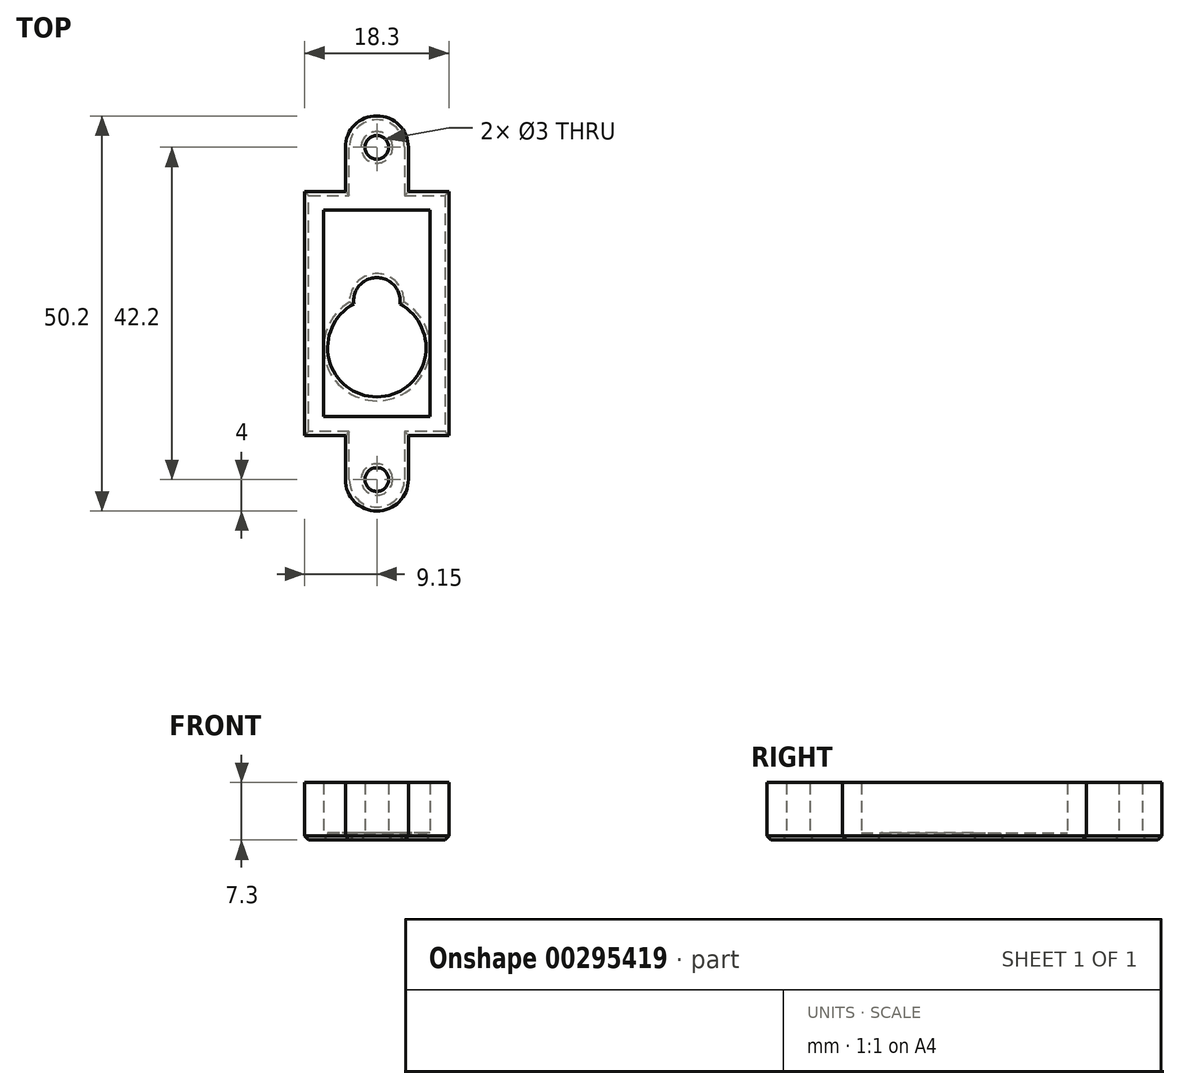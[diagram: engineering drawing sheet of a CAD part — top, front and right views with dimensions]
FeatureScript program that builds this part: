
annotation { "Feature Type Name" : "Feature", "Feature Type Description" : "" }
export const myFeature = defineFeature(function(context is Context, id is Id, definition is map)
    precondition{}
    {
        {
            var Q0;
            Q0=qCreatedBy(makeId("Top.planeOp"),FACE);
            var sketch = newSketch(context, id + "F0", { "sketchPlane" : qUnion([Q0])});
            skLineSegment(sketch, "E0.bottom", {"start": v(6.75, -13.1) * mm, "end": v(-6.75, -13.1) * mm});
            skLineSegment(sketch, "E0.top", {"start": v(6.75, 13.1) * mm, "end": v(-6.75, 13.1) * mm});
            skLineSegment(sketch, "E0.left", {"start": v(6.75, -13.1) * mm, "end": v(6.75, 13.1) * mm});
            skLineSegment(sketch, "E0.right", {"start": v(-6.75, -13.1) * mm, "end": v(-6.75, 13.1) * mm});
            skPoint(sketch, "E0.middle", {"position": v(0, 0) * mm});
            skLineSegment(sketch, "E1", {"start": v(-6.75, -11) * mm, "end": v(6.75, -11) * mm, "construction": true});
            skLineSegment(sketch, "E2", {"start": v(-6.75, 11) * mm, "end": v(6.75, 11) * mm, "construction": true});
            skArc(sketch, "E3", {"start": v(-2.92, 1.18) * mm, "mid": v(0, -10.6) * mm, "end": v(2.92, 1.18) * mm});
            skArc(sketch, "E4", {"start": v(2.92, 1.18) * mm, "mid": v(0, 4.55) * mm, "end": v(-2.92, 1.18) * mm});
            skSolve(sketch);
        }
        {
            var Q0;
            Q0 = qSketchRegion(id + "F0", true);
            extrude(context, id + "F1", {"entities" : qUnion([Q0]), "depth" : 2 * mm});
        }
        {
            var Q0;
            Q0=qCreatedBy(makeId("Top.planeOp"),FACE);
            var sketch = newSketch(context, id + "F2", { "sketchPlane" : qUnion([Q0])});
            skLineSegment(sketch, "E5", {"start": v(9.15, 15.5) * mm, "end": v(9.15, -15.5) * mm});
            skLineSegment(sketch, "E6", {"start": v(-9.15, 15.5) * mm, "end": v(-9.15, -15.5) * mm});
            skLineSegment(sketch, "E7", {"start": v(-9.15, 15.5) * mm, "end": v(9.15, 15.5) * mm});
            skLineSegment(sketch, "E8", {"start": v(9.15, -15.5) * mm, "end": v(-9.15, -15.5) * mm});
            skLineSegment(sketch, "E9.0", {"start": v(6.75, -13.1) * mm, "end": v(-6.75, -13.1) * mm});
            skLineSegment(sketch, "E10.0", {"start": v(6.75, -13.1) * mm, "end": v(6.75, 13.1) * mm});
            skLineSegment(sketch, "E11.0", {"start": v(6.75, 13.1) * mm, "end": v(-6.75, 13.1) * mm});
            skLineSegment(sketch, "E12.0", {"start": v(-6.75, -13.1) * mm, "end": v(-6.75, 13.1) * mm});
            skSolve(sketch);
        }
        {
            var Q0;
            Q0 = qSketchRegion(id + "F2", true);
            extrude(context, id + "F3", {"entities" : qUnion([Q0]), "operationType" : NewBodyOperationType.ADD, "depth" : (2 + 6.4) * mm});
        }
        {
            var Q0;
            Q0=qCreatedBy(makeId("Top.planeOp"),FACE);
            var sketch = newSketch(context, id + "F4", { "sketchPlane" : qUnion([Q0])});
            skLineSegment(sketch, "E13.0", {"start": v(-9.15, 15.5) * mm, "end": v(9.15, 15.5) * mm});
            skLineSegment(sketch, "E14.0", {"start": v(4, -15.5) * mm, "end": v(-4, -15.5) * mm});
            skLineSegment(sketch, "E15.0", {"start": v(9.15, -17.1) * mm, "end": v(4, -17.1) * mm, "construction": true});
            skArc(sketch, "E16", {"start": v(-4, -21.1) * mm, "mid": v(0, -25.1) * mm, "end": v(4, -21.1) * mm});
            skLineSegment(sketch, "E17", {"start": v(4, -15.5) * mm, "end": v(4, -21.1) * mm});
            skLineSegment(sketch, "E18", {"start": v(-4, -15.5) * mm, "end": v(-4, -21.1) * mm});
            skPoint(sketch, "E19.orphan", {"position": v(9.15, -15.5) * mm});
            skPoint(sketch, "E20.orphan", {"position": v(-9.15, -15.5) * mm});
            skLineSegment(sketch, "E21.MirrorCS", {"start": v(4, 15.5) * mm, "end": v(-4, 15.5) * mm});
            skArc(sketch, "E22.MirrorCS", {"start": v(-4, 21.1) * mm, "mid": v(0, 25.1) * mm, "end": v(4, 21.1) * mm});
            skLineSegment(sketch, "E23.MirrorCS", {"start": v(4, 15.5) * mm, "end": v(4, 21.1) * mm});
            skLineSegment(sketch, "E24.MirrorCS", {"start": v(-4, 15.5) * mm, "end": v(-4, 21.1) * mm});
            skCircle(sketch, "E25", {"center": v(0, 21.1) * mm, "radius": 1.5 * mm});
            skCircle(sketch, "E26", {"center": v(0, -21.1) * mm, "radius": 1.5 * mm});
            skSolve(sketch);
        }
        {
            var Q0;
            Q0 = qSketchRegion(id + "F4", true);
            var Q1;
            Q1=makeQuery(id+"F3.opExtrude","CAP_FACE",FACE,{"disambiguationData":[OSD([sQuery(id+"F2.wireOp",EDGE,"E5"),sQuery(id+"F2.wireOp",EDGE,"E6"),sQuery(id+"F2.wireOp",EDGE,"E7"),sQuery(id+"F2.wireOp",EDGE,"E8"),sQuery(id+"F2.wireOp",EDGE,"E9.0"),sQuery(id+"F2.wireOp",EDGE,"E10.0"),sQuery(id+"F2.wireOp",EDGE,"E11.0"),sQuery(id+"F2.wireOp",EDGE,"E12.0")])],"isStart":false});
            extrude(context, id + "F5", {"entities" : qUnion([Q0]), "operationType" : NewBodyOperationType.ADD, "endBound" : BoundingType.UP_TO_SURFACE, "endBoundEntityFace" : qUnion([Q1]), "depth" : 25 * mm});
        }
        {
            var Q0;
            Q0=makeQuery(id+"F5.boolean.opBoolean","MERGE",FACE,{"derivedFrom":[makeQuery(id+"F3.boolean.opBoolean","MERGE",FACE,{"derivedFrom":[makeQuery(id+"F1.opExtrude","CAP_FACE",FACE,{"disambiguationData":[OSD([sQuery(id+"F0.wireOp",EDGE,"E0.bottom"),sQuery(id+"F0.wireOp",EDGE,"E0.top"),sQuery(id+"F0.wireOp",EDGE,"E0.left"),sQuery(id+"F0.wireOp",EDGE,"E0.right"),sQuery(id+"F0.wireOp",EDGE,"E3"),sQuery(id+"F0.wireOp",EDGE,"E4")])],"isStart":true}),makeQuery(id+"F3.opExtrude","CAP_FACE",FACE,{"disambiguationData":[OSD([sQuery(id+"F2.wireOp",EDGE,"E5"),sQuery(id+"F2.wireOp",EDGE,"E6"),sQuery(id+"F2.wireOp",EDGE,"E7"),sQuery(id+"F2.wireOp",EDGE,"E8"),sQuery(id+"F2.wireOp",EDGE,"E9.0"),sQuery(id+"F2.wireOp",EDGE,"E10.0"),sQuery(id+"F2.wireOp",EDGE,"E11.0"),sQuery(id+"F2.wireOp",EDGE,"E12.0")])],"isStart":true})]}),makeQuery(id+"F5.opExtrude","CAP_FACE",FACE,{"disambiguationData":[OSD([sQuery(id+"F4.wireOp",EDGE,"E14.0"),sQuery(id+"F4.wireOp",EDGE,"E16"),sQuery(id+"F4.wireOp",EDGE,"E17"),sQuery(id+"F4.wireOp",EDGE,"E18"),sQuery(id+"F4.wireOp",EDGE,"E26")])],"isStart":true}),makeQuery(id+"F5.opExtrude","CAP_FACE",FACE,{"disambiguationData":[OSD([sQuery(id+"F4.wireOp",EDGE,"E21.MirrorCS"),sQuery(id+"F4.wireOp",EDGE,"E22.MirrorCS"),sQuery(id+"F4.wireOp",EDGE,"E23.MirrorCS"),sQuery(id+"F4.wireOp",EDGE,"E24.MirrorCS"),sQuery(id+"F4.wireOp",EDGE,"E25")])],"isStart":true})]});
            extrude(context, id + "F6", {"entities" : qUnion([Q0]), "operationType" : NewBodyOperationType.ADD, "depth" : 2.4 * mm});
        }
        {
            var Q0;
            Q0=makeQuery(id+"F6.opExtrude","CAP_FACE",FACE,{"disambiguationData":[OSD([sQuery(id+"F0.wireOp",EDGE,"E0.bottom"),sQuery(id+"F0.wireOp",EDGE,"E0.top"),sQuery(id+"F0.wireOp",EDGE,"E0.left"),sQuery(id+"F0.wireOp",EDGE,"E0.right"),sQuery(id+"F0.wireOp",EDGE,"E3"),sQuery(id+"F0.wireOp",EDGE,"E4"),sQuery(id+"F2.wireOp",EDGE,"E5"),sQuery(id+"F2.wireOp",EDGE,"E6"),sQuery(id+"F2.wireOp",EDGE,"E7"),sQuery(id+"F2.wireOp",EDGE,"E8"),sQuery(id+"F2.wireOp",EDGE,"E9.0"),sQuery(id+"F2.wireOp",EDGE,"E10.0"),sQuery(id+"F2.wireOp",EDGE,"E11.0"),sQuery(id+"F2.wireOp",EDGE,"E12.0"),sQuery(id+"F4.wireOp",EDGE,"E14.0"),sQuery(id+"F4.wireOp",EDGE,"E16"),sQuery(id+"F4.wireOp",EDGE,"E17"),sQuery(id+"F4.wireOp",EDGE,"E18"),sQuery(id+"F4.wireOp",EDGE,"E21.MirrorCS"),sQuery(id+"F4.wireOp",EDGE,"E22.MirrorCS"),sQuery(id+"F4.wireOp",EDGE,"E23.MirrorCS"),sQuery(id+"F4.wireOp",EDGE,"E24.MirrorCS"),sQuery(id+"F4.wireOp",EDGE,"E25"),sQuery(id+"F4.wireOp",EDGE,"E26")])],"isStart":false});
            extrude(context, id + "F7", {"entities" : qUnion([Q0]), "operationType" : NewBodyOperationType.REMOVE, "oppositeDirection" : true, "depth" : 2 * mm});
        }
        {
            var Q0;
            Q0=makeQuery(id+"F7.boolean.opBoolean","COPY",FACE,{"derivedFrom":makeQuery(id+"F7.opExtrude","CAP_FACE",FACE,{"disambiguationData":[OSD([sQuery(id+"F0.wireOp",EDGE,"E0.bottom"),sQuery(id+"F0.wireOp",EDGE,"E0.top"),sQuery(id+"F0.wireOp",EDGE,"E0.left"),sQuery(id+"F0.wireOp",EDGE,"E0.right"),sQuery(id+"F0.wireOp",EDGE,"E3"),sQuery(id+"F0.wireOp",EDGE,"E4"),sQuery(id+"F2.wireOp",EDGE,"E5"),sQuery(id+"F2.wireOp",EDGE,"E6"),sQuery(id+"F2.wireOp",EDGE,"E7"),sQuery(id+"F2.wireOp",EDGE,"E8"),sQuery(id+"F2.wireOp",EDGE,"E9.0"),sQuery(id+"F2.wireOp",EDGE,"E10.0"),sQuery(id+"F2.wireOp",EDGE,"E11.0"),sQuery(id+"F2.wireOp",EDGE,"E12.0"),sQuery(id+"F4.wireOp",EDGE,"E14.0"),sQuery(id+"F4.wireOp",EDGE,"E16"),sQuery(id+"F4.wireOp",EDGE,"E17"),sQuery(id+"F4.wireOp",EDGE,"E18"),sQuery(id+"F4.wireOp",EDGE,"E21.MirrorCS"),sQuery(id+"F4.wireOp",EDGE,"E22.MirrorCS"),sQuery(id+"F4.wireOp",EDGE,"E23.MirrorCS"),sQuery(id+"F4.wireOp",EDGE,"E24.MirrorCS"),sQuery(id+"F4.wireOp",EDGE,"E25"),sQuery(id+"F4.wireOp",EDGE,"E26")])],"isStart":false})});
            extrude(context, id + "F8", {"entities" : qUnion([Q0]), "operationType" : NewBodyOperationType.REMOVE, "oppositeDirection" : true, "depth" : 2 * mm});
        }
        {
            var Q0;
            Q0=makeQuery(id+"F8.boolean.opBoolean","COPY",FACE,{"derivedFrom":makeQuery(id+"F8.opExtrude","CAP_FACE",FACE,{"disambiguationData":[OSD([sQuery(id+"F0.wireOp",EDGE,"E0.bottom"),sQuery(id+"F0.wireOp",EDGE,"E0.top"),sQuery(id+"F0.wireOp",EDGE,"E0.left"),sQuery(id+"F0.wireOp",EDGE,"E0.right"),sQuery(id+"F0.wireOp",EDGE,"E3"),sQuery(id+"F0.wireOp",EDGE,"E4"),sQuery(id+"F2.wireOp",EDGE,"E5"),sQuery(id+"F2.wireOp",EDGE,"E6"),sQuery(id+"F2.wireOp",EDGE,"E7"),sQuery(id+"F2.wireOp",EDGE,"E8"),sQuery(id+"F2.wireOp",EDGE,"E9.0"),sQuery(id+"F2.wireOp",EDGE,"E10.0"),sQuery(id+"F2.wireOp",EDGE,"E11.0"),sQuery(id+"F2.wireOp",EDGE,"E12.0"),sQuery(id+"F4.wireOp",EDGE,"E14.0"),sQuery(id+"F4.wireOp",EDGE,"E16"),sQuery(id+"F4.wireOp",EDGE,"E17"),sQuery(id+"F4.wireOp",EDGE,"E18"),sQuery(id+"F4.wireOp",EDGE,"E21.MirrorCS"),sQuery(id+"F4.wireOp",EDGE,"E22.MirrorCS"),sQuery(id+"F4.wireOp",EDGE,"E23.MirrorCS"),sQuery(id+"F4.wireOp",EDGE,"E24.MirrorCS"),sQuery(id+"F4.wireOp",EDGE,"E25"),sQuery(id+"F4.wireOp",EDGE,"E26")])],"isStart":false})});
            extrude(context, id + "F9", {"entities" : qUnion([Q0]), "operationType" : NewBodyOperationType.ADD, "depth" : 1 * mm});
        }
        {
            var Q0;
            Q0=makeQuery(id+"F9.opExtrude","CAP_FACE",FACE,{"disambiguationData":[OSD([sQuery(id+"F0.wireOp",EDGE,"E0.bottom"),sQuery(id+"F0.wireOp",EDGE,"E0.top"),sQuery(id+"F0.wireOp",EDGE,"E0.left"),sQuery(id+"F0.wireOp",EDGE,"E0.right"),sQuery(id+"F0.wireOp",EDGE,"E3"),sQuery(id+"F0.wireOp",EDGE,"E4"),sQuery(id+"F2.wireOp",EDGE,"E5"),sQuery(id+"F2.wireOp",EDGE,"E6"),sQuery(id+"F2.wireOp",EDGE,"E7"),sQuery(id+"F2.wireOp",EDGE,"E8"),sQuery(id+"F2.wireOp",EDGE,"E9.0"),sQuery(id+"F2.wireOp",EDGE,"E10.0"),sQuery(id+"F2.wireOp",EDGE,"E11.0"),sQuery(id+"F2.wireOp",EDGE,"E12.0"),sQuery(id+"F4.wireOp",EDGE,"E14.0"),sQuery(id+"F4.wireOp",EDGE,"E16"),sQuery(id+"F4.wireOp",EDGE,"E17"),sQuery(id+"F4.wireOp",EDGE,"E18"),sQuery(id+"F4.wireOp",EDGE,"E21.MirrorCS"),sQuery(id+"F4.wireOp",EDGE,"E22.MirrorCS"),sQuery(id+"F4.wireOp",EDGE,"E23.MirrorCS"),sQuery(id+"F4.wireOp",EDGE,"E24.MirrorCS"),sQuery(id+"F4.wireOp",EDGE,"E25"),sQuery(id+"F4.wireOp",EDGE,"E26")])],"isStart":false});
            extrude(context, id + "F10", {"entities" : qUnion([Q0]), "operationType" : NewBodyOperationType.REMOVE, "oppositeDirection" : true, "depth" : 0.5 * mm});
        }
        {
            var Q0;
            Q0=makeQuery(id+"F10.boolean.opBoolean","COPY",FACE,{"derivedFrom":makeQuery(id+"F10.opExtrude","CAP_FACE",FACE,{"disambiguationData":[OSD([sQuery(id+"F0.wireOp",EDGE,"E0.bottom"),sQuery(id+"F0.wireOp",EDGE,"E0.top"),sQuery(id+"F0.wireOp",EDGE,"E0.left"),sQuery(id+"F0.wireOp",EDGE,"E0.right"),sQuery(id+"F0.wireOp",EDGE,"E3"),sQuery(id+"F0.wireOp",EDGE,"E4"),sQuery(id+"F2.wireOp",EDGE,"E5"),sQuery(id+"F2.wireOp",EDGE,"E6"),sQuery(id+"F2.wireOp",EDGE,"E7"),sQuery(id+"F2.wireOp",EDGE,"E8"),sQuery(id+"F2.wireOp",EDGE,"E9.0"),sQuery(id+"F2.wireOp",EDGE,"E10.0"),sQuery(id+"F2.wireOp",EDGE,"E11.0"),sQuery(id+"F2.wireOp",EDGE,"E12.0"),sQuery(id+"F4.wireOp",EDGE,"E14.0"),sQuery(id+"F4.wireOp",EDGE,"E16"),sQuery(id+"F4.wireOp",EDGE,"E17"),sQuery(id+"F4.wireOp",EDGE,"E18"),sQuery(id+"F4.wireOp",EDGE,"E21.MirrorCS"),sQuery(id+"F4.wireOp",EDGE,"E22.MirrorCS"),sQuery(id+"F4.wireOp",EDGE,"E23.MirrorCS"),sQuery(id+"F4.wireOp",EDGE,"E24.MirrorCS"),sQuery(id+"F4.wireOp",EDGE,"E25"),sQuery(id+"F4.wireOp",EDGE,"E26")])],"isStart":false})});
            chamfer(context, id + "F11", {"entities" : qUnion([Q0]), "width" : 0.5 * mm, "tangentPropagation" : true});
        }
    });
